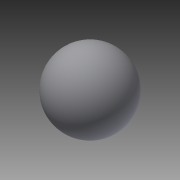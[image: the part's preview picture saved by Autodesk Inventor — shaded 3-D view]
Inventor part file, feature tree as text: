
AUTODESK INVENTOR PART (.ipt)
format: ipt  version: 2015 (Build 190159000, 159)  size: 98,816 bytes
history: native  units: mm
features: revolve x1, sketch x1
ambient origin geometry x8: Origin, YZ Plane, XZ Plane, XY Plane, X Axis, Y Axis, Z Axis, Center Point
bodies: Solid1 (feature_tree)
feature tree (2):
  revolve  "Revolution1"  [1 undecoded]
  sketch  "Sketch1"  dims[d0=220.0mm d1=3.490659mm]
note: 1 required parameter value undecoded (feature->parameter linkage not recoverable at this tier; creation-order binding heuristic only, values carry confidence <= 0.55)
